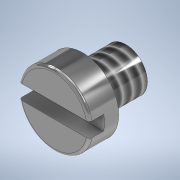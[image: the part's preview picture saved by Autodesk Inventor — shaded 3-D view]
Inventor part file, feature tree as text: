
AUTODESK INVENTOR PART (.ipt)
format: ipt  version: 2021 (Build 250183000, 183)  size: 147,968 bytes
history: native  units: mm
features: extrude x4, sketch x4, other x1, fillet x1, thread x1
ambient origin geometry x8: Origin, YZ Plane, XZ Plane, XY Plane, X Axis, Y Axis, Z Axis, Center Point
bodies: Body1 (feature_tree)
feature tree (11):
  other  "Sólido1"
  extrude  "Extrusão1"  Depth=1.0mm TaperAngle=0.0deg
  extrude  "Extrusão2"  Depth=1.5mm TaperAngle=0.0deg
  extrude  "Extrusão3"  Depth=0.5mm TaperAngle=0.0deg
  extrude  "Extrusão4"  Depth=0.1mm
  fillet  "Arredondamento1"  Radius=0.1mm
  thread  "Rosca1"  [1 undecoded]
  sketch  "Esboço1"  dims[d0=2.5mm d1=1.0mm d2=0.0mm]
  sketch  "Esboço2"  dims[d3=1.5mm d4=1.5mm d5=0.0mm]
  sketch  "Esboço3"  dims[d6=2.448289mm d7=0.5mm d8=0.0mm]
  sketch  "Esboço4"  dims[d9=6.0mm d10=0.0mm d11=0.1mm d12=0.1mm d13=15.255mm d14=0.0mm]
note: 1 required parameter value undecoded (feature->parameter linkage not recoverable at this tier; creation-order binding heuristic only, values carry confidence <= 0.55)
